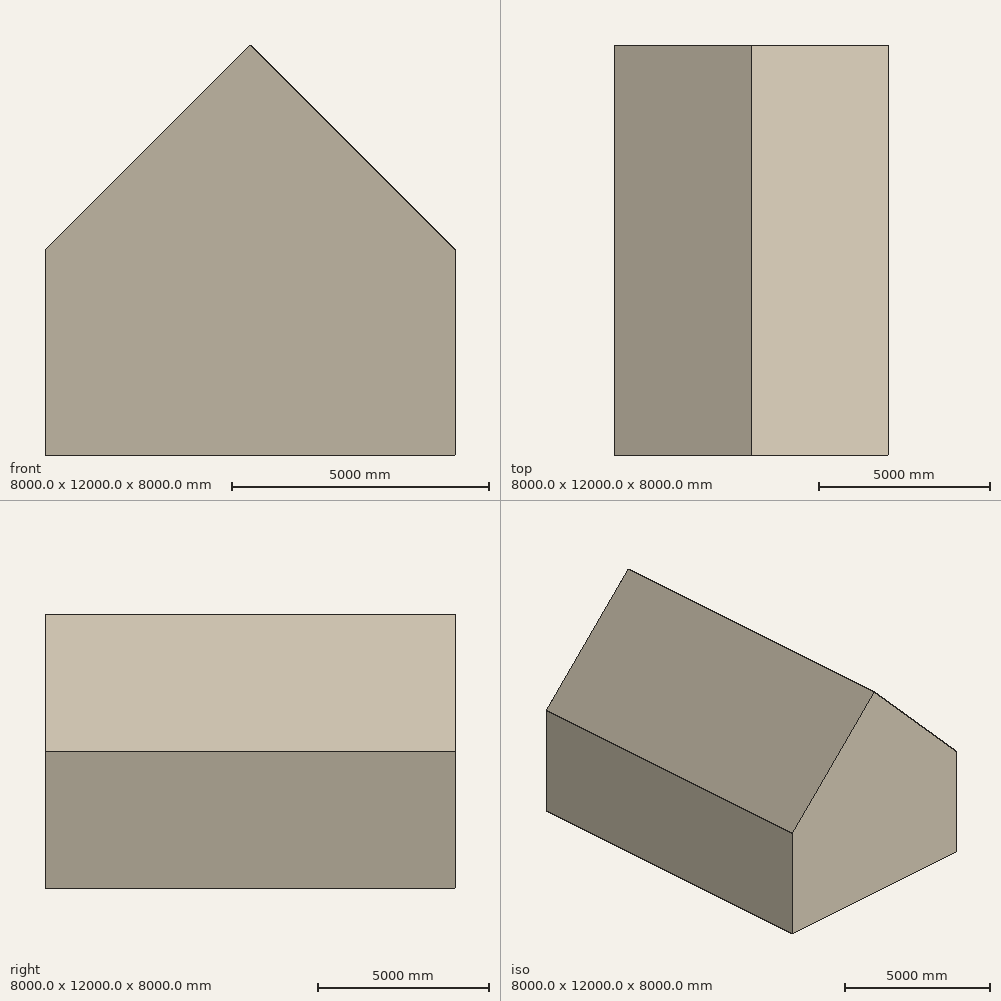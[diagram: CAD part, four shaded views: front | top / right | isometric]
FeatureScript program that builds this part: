
annotation { "Feature Type Name" : "Feature", "Feature Type Description" : "" }
export const myFeature = defineFeature(function(context is Context, id is Id, definition is map)
    precondition{}
    {
        {
            var Q0;
            Q0=qCreatedBy(makeId("Front.planeOp"),FACE);
            var sketch = newSketch(context, id + "F0", { "sketchPlane" : qUnion([Q0])});
            skLineSegment(sketch, "E0.bottom", {"start": v(-3998.4, 5842.5) * mm, "end": v(4001.6, 5842.5) * mm});
            skLineSegment(sketch, "E0.top", {"start": v(-3998.4, -2157.5) * mm, "end": v(4001.6, -2157.5) * mm});
            skLineSegment(sketch, "E0.left", {"start": v(-3998.4, 5842.5) * mm, "end": v(-3998.4, -2157.5) * mm});
            skLineSegment(sketch, "E0.right", {"start": v(4001.6, 5842.5) * mm, "end": v(4001.6, -2157.5) * mm});
            skSolve(sketch);
        }
        {
            var Q0;
            Q0 = qSketchRegion(id + "F0", true);
            extrude(context, id + "F1", {"entities" : qUnion([Q0]), "depth" : 12000 * mm});
        }
        {
            var Q0;
            Q0=makeQuery(id+"F1.opExtrude","CAP_FACE",FACE,{"disambiguationData":[OSD([sQuery(id+"F0.wireOp",EDGE,"E0.bottom"),sQuery(id+"F0.wireOp",EDGE,"E0.top"),sQuery(id+"F0.wireOp",EDGE,"E0.left"),sQuery(id+"F0.wireOp",EDGE,"E0.right")])],"isStart":false});
            var sketch = newSketch(context, id + "F2", { "sketchPlane" : qUnion([Q0])});
            skLineSegment(sketch, "E1", {"start": v(-3998.4, 1842.5) * mm, "end": v(1.6, 5842.5) * mm});
            skLineSegment(sketch, "E2", {"start": v(1.6, 5842.5) * mm, "end": v(4001.6, 1842.5) * mm});
            skSolve(sketch);
        }
        {
            var Q0;
            Q0 = qSketchRegion(id + "F2", true);
            var Q1;
            {var subQ0=sQuery(id+"F2.wireOp",EDGE,"E1");Q1=makeQuery(id+"F2.imprint","IMPRINT",FACE,{"disambiguationData":[TD([[makeQuery(id+"F2.imprint","IMPRINT",EDGE,{"derivedFrom":subQ0}),1.0]])]});}
            var Q2;
            {var subQ0=sQuery(id+"F2.wireOp",EDGE,"E2");Q2=makeQuery(id+"F2.imprint","IMPRINT",FACE,{"disambiguationData":[TD([[makeQuery(id+"F2.imprint","IMPRINT",EDGE,{"derivedFrom":subQ0}),1.0]])]});}
            extrude(context, id + "F3", {"entities" : qUnion([Q0, Q1, Q2]), "operationType" : NewBodyOperationType.REMOVE, "endBound" : BoundingType.THROUGH_ALL, "oppositeDirection" : true, "depth" : 25 * mm});
        }
    });
